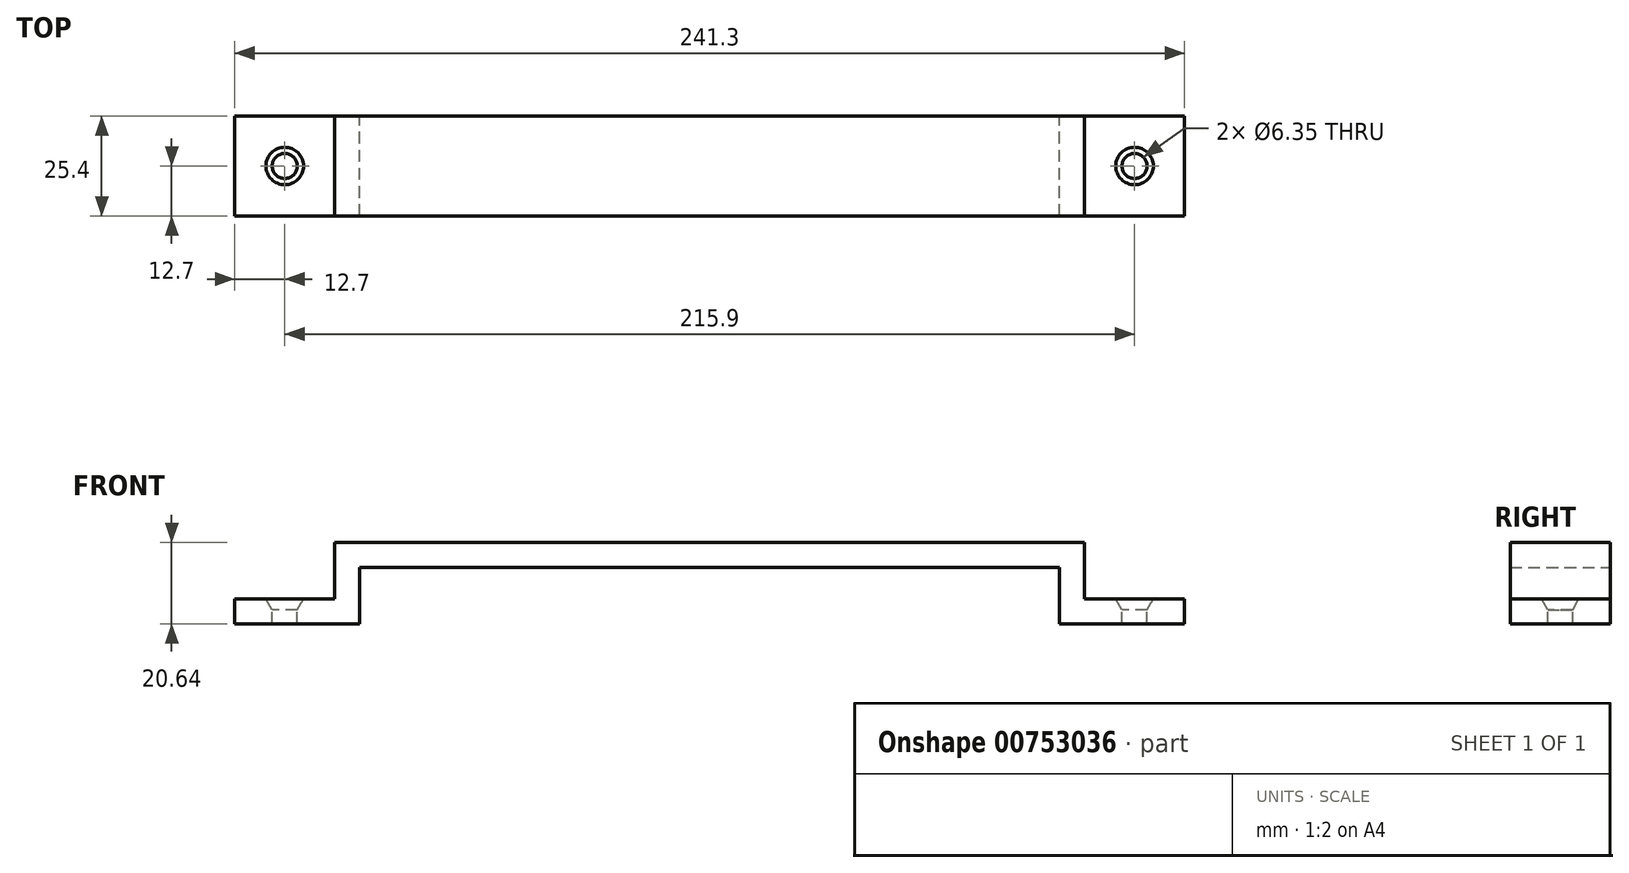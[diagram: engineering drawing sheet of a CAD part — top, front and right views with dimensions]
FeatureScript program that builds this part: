
annotation { "Feature Type Name" : "Feature", "Feature Type Description" : "" }
export const myFeature = defineFeature(function(context is Context, id is Id, definition is map)
    precondition{}
    {
        {
            var Q0;
            Q0=qCreatedBy(makeId("Top.planeOp"),FACE);
            var sketch = newSketch(context, id + "F0", { "sketchPlane" : qUnion([Q0])});
            skLineSegment(sketch, "E0.bottom", {"start": v(0, 25.4) * mm, "end": v(177.8, 25.4) * mm});
            skLineSegment(sketch, "E0.top", {"start": v(0, 0) * mm, "end": v(177.8, 0) * mm});
            skLineSegment(sketch, "E0.left", {"start": v(0, 25.4) * mm, "end": v(0, 0) * mm});
            skLineSegment(sketch, "E0.right", {"start": v(177.8, 25.4) * mm, "end": v(177.8, 0) * mm});
            skSolve(sketch);
        }
        {
            var Q0;
            Q0=qCreatedBy(makeId("Front.planeOp"),FACE);
            var sketch = newSketch(context, id + "F1", { "sketchPlane" : qUnion([Q0])});
            skLineSegment(sketch, "E1.0", {"start": v(0, 0) * mm, "end": v(177.8, 0) * mm});
            skLineSegment(sketch, "E2", {"start": v(177.8, 0) * mm, "end": v(177.8, -15.88) * mm});
            skLineSegment(sketch, "E3", {"start": v(177.8, -15.88) * mm, "end": v(0, -15.88) * mm});
            skLineSegment(sketch, "E4", {"start": v(0, -15.88) * mm, "end": v(0, 0) * mm});
            skSolve(sketch);
        }
        {
            var Q0;
            Q0=qCreatedBy(makeId("Front.planeOp"),FACE);
            var sketch = newSketch(context, id + "F2", { "sketchPlane" : qUnion([Q0])});
            skLineSegment(sketch, "E5", {"start": v(-31.75, -14.29) * mm, "end": v(-31.75, -7.94) * mm});
            skLineSegment(sketch, "E6", {"start": v(-31.75, -7.94) * mm, "end": v(-6.35, -7.94) * mm});
            skLineSegment(sketch, "E7", {"start": v(-6.35, -7.94) * mm, "end": v(-6.35, 6.35) * mm});
            skLineSegment(sketch, "E8", {"start": v(-6.35, 6.35) * mm, "end": v(184.15, 6.35) * mm});
            skLineSegment(sketch, "E9", {"start": v(184.15, 6.35) * mm, "end": v(184.15, -7.94) * mm});
            skLineSegment(sketch, "E10", {"start": v(184.15, -7.94) * mm, "end": v(209.55, -7.94) * mm});
            skLineSegment(sketch, "E11", {"start": v(209.55, -7.94) * mm, "end": v(209.55, -14.29) * mm});
            skLineSegment(sketch, "E12.0", {"start": v(0, -14.29) * mm, "end": v(0, 0) * mm});
            skLineSegment(sketch, "E13.0", {"start": v(0, 0) * mm, "end": v(177.8, 0) * mm});
            skLineSegment(sketch, "E14.0", {"start": v(177.8, 0) * mm, "end": v(177.8, -14.29) * mm});
            skLineSegment(sketch, "E15", {"start": v(-31.75, -14.29) * mm, "end": v(0, -14.29) * mm});
            skLineSegment(sketch, "E16", {"start": v(177.8, -14.29) * mm, "end": v(209.55, -14.29) * mm});
            skPoint(sketch, "E17.orphan", {"position": v(0, -15.88) * mm});
            skPoint(sketch, "E18.orphan", {"position": v(177.8, -15.88) * mm});
            skSolve(sketch);
        }
        {
            var Q0;
            Q0 = qSketchRegion(id + "F2", true);
            extrude(context, id + "F3", {"entities" : qUnion([Q0]), "endBound" : BoundingType.SYMMETRIC, "depth" : 25.4 * mm, "offsetDistance" : 25.4 * mm});
        }
        {
            var Q0;
            Q0=makeQuery(id+"F3.opExtrude","SWEPT_FACE",FACE,{"disambiguationData":[OSD([sQuery(id+"F2.wireOp",EDGE,"E6")])]});
            var sketch = newSketch(context, id + "F4", { "sketchPlane" : qUnion([Q0])});
            skPoint(sketch, "E19", {"position": v(-19.05, 0) * mm});
            skPoint(sketch, "E20", {"position": v(196.85, 0) * mm});
            skLineSegment(sketch, "E21", {"start": v(-31.75, 0) * mm, "end": v(-19.05, 0) * mm, "construction": true});
            skLineSegment(sketch, "E22", {"start": v(196.85, 0) * mm, "end": v(209.55, 0) * mm, "construction": true});
            skSolve(sketch);
        }
        {
            var Q0;
            Q0=sQuery(id+"F4.wireOp",VERTEX,"E19");
            var Q1;
            Q1=sQuery(id+"F4.wireOp",VERTEX,"E20");
            var Q2;
            Q2=makeQuery(id+"F3.opExtrude","SWEPT_BODY",BODY,{"disambiguationData":[OSD([sQuery(id+"F2.wireOp",EDGE,"E5"),sQuery(id+"F2.wireOp",EDGE,"E6"),sQuery(id+"F2.wireOp",EDGE,"E7"),sQuery(id+"F2.wireOp",EDGE,"E8"),sQuery(id+"F2.wireOp",EDGE,"E9"),sQuery(id+"F2.wireOp",EDGE,"E10"),sQuery(id+"F2.wireOp",EDGE,"E11"),sQuery(id+"F2.wireOp",EDGE,"E12.0"),sQuery(id+"F2.wireOp",EDGE,"E13.0"),sQuery(id+"F2.wireOp",EDGE,"E14.0"),sQuery(id+"F2.wireOp",EDGE,"E15"),sQuery(id+"F2.wireOp",EDGE,"E16")])]});
            hole(context, id + "F5", {"style" : HoleStyle.C_SINK, "endStyle" : HoleEndStyle.THROUGH, "holeDiameter" : 6.35 * mm, "cSinkDiameter" : 9.52 * mm, "cSinkAngle" : 60 * degree, "majorDiameter" : 6.35 * mm, "isTappedThrough" : true, "tappedDepth" : 12.7 * mm, "tapClearance" : 3, "locations" : qUnion([Q0, Q1]), "scope" : qUnion([Q2])});
        }
    });
